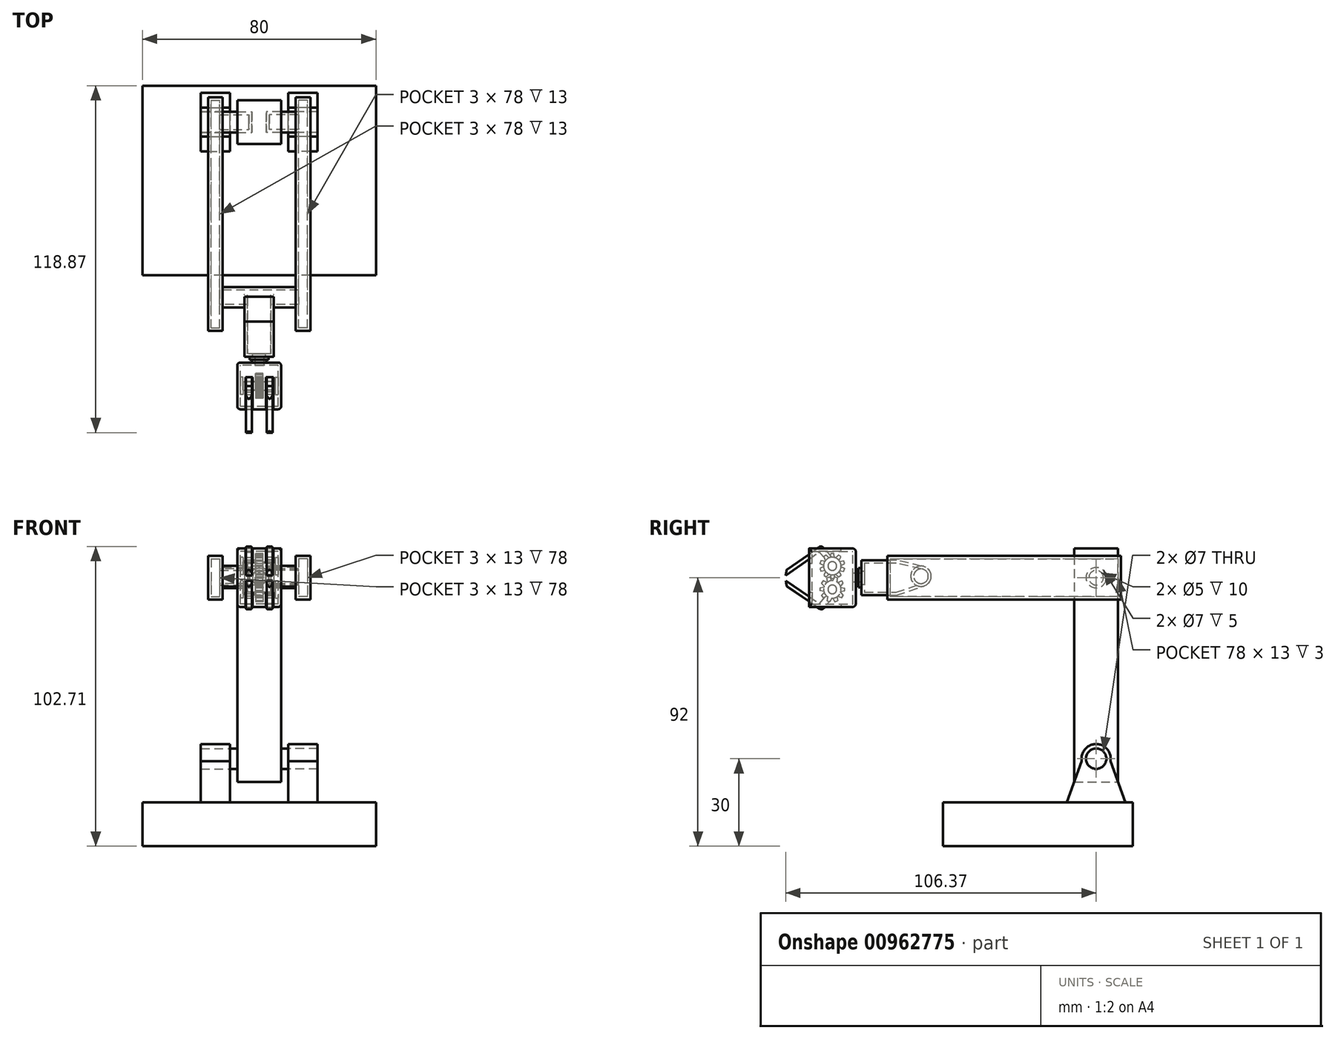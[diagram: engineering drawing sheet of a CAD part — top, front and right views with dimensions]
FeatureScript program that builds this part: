
annotation { "Feature Type Name" : "Feature", "Feature Type Description" : "" }
export const myFeature = defineFeature(function(context is Context, id is Id, definition is map)
    precondition{}
    {
        {
            var Q0;
            Q0=qCreatedBy(makeId("Top.planeOp"),FACE);
            var sketch = newSketch(context, id + "F0", { "sketchPlane" : qUnion([Q0])});
            skLineSegment(sketch, "E0.bottom", {"start": v(40, -32.5) * mm, "end": v(-40, -32.5) * mm});
            skLineSegment(sketch, "E0.top", {"start": v(40, 32.5) * mm, "end": v(-40, 32.5) * mm});
            skLineSegment(sketch, "E0.left", {"start": v(40, -32.5) * mm, "end": v(40, 32.5) * mm});
            skLineSegment(sketch, "E0.right", {"start": v(-40, -32.5) * mm, "end": v(-40, 32.5) * mm});
            skPoint(sketch, "E0.middle", {"position": v(0, 0) * mm});
            skSolve(sketch);
        }
        {
            var Q0;
            Q0=qSketchRegion(id+"F0",true);
            extrude(context, id + "F1", {"entities" : qUnion([Q0]), "depth" : 15 * mm, "offsetDistance" : 25 * mm});
        }
        {
            var Q0;
            Q0=qCreatedBy(makeId("Right.planeOp"),FACE);
            cPlane(context, id + "F2", {"entities" : qUnion([Q0]), "cplaneType" : CPlaneType.OFFSET, "offset" : 10 * mm, "width" : 150 * mm, "height" : 150 * mm});
        }
        {
            var Q0;
            Q0=qCreatedBy(id+"F2.planeOp",FACE);
            var sketch = newSketch(context, id + "F3", { "sketchPlane" : qUnion([Q0])});
            skCircle(sketch, "E1", {"center": v(20, 30) * mm, "radius": 5 * mm});
            skLineSegment(sketch, "E2", {"start": v(15.08, 29.11) * mm, "end": v(10, 15) * mm});
            skLineSegment(sketch, "E3", {"start": v(20, 30) * mm, "end": v(20, 15) * mm, "construction": true});
            skLineSegment(sketch, "E4.MirrorCS", {"start": v(24.92, 29.11) * mm, "end": v(30, 15) * mm});
            skLineSegment(sketch, "E5", {"start": v(10, 15) * mm, "end": v(30, 15) * mm});
            skCircle(sketch, "E6", {"center": v(20, 30) * mm, "radius": 3.5 * mm});
            skSolve(sketch);
        }
        {
            var Q0;
            Q0=qSketchRegion(id+"F3",true);
            extrude(context, id + "F4", {"entities" : qUnion([Q0]), "depth" : 10 * mm, "offsetDistance" : 25 * mm});
        }
        {
            var Q0;
            Q0=makeQuery(id+"F4.opExtrude","SWEPT_BODY",BODY,{"disambiguationData":[OSD([sQuery(id+"F3.wireOp",EDGE,"E1"),sQuery(id+"F3.wireOp",EDGE,"E2"),sQuery(id+"F3.wireOp",EDGE,"E4.MirrorCS"),sQuery(id+"F3.wireOp",EDGE,"E5"),sQuery(id+"F3.wireOp",EDGE,"E6")])]});
            var Q1;
            Q1=qCreatedBy(makeId("Right.planeOp"),FACE);
            mirror(context, id + "F5", {"operationType" : NewBodyOperationType.ADD, "entities" : qUnion([Q0]), "mirrorPlane" : qUnion([Q1])});
        }
        {
            var Q0;
            Q0=qCreatedBy(makeId("Right.planeOp"),FACE);
            var sketch = newSketch(context, id + "F6", { "sketchPlane" : qUnion([Q0])});
            skCircle(sketch, "E7.0", {"center": v(20, 30) * mm, "radius": 3.5 * mm});
            skSolve(sketch);
        }
        {
            var Q0;
            Q0=qSketchRegion(id+"F6",true);
            extrude(context, id + "F7", {"entities" : qUnion([Q0]), "endBound" : BoundingType.SYMMETRIC, "depth" : 40 * mm, "offsetDistance" : 25 * mm});
        }
        {
            var Q0;
            Q0=qCreatedBy(makeId("Right.planeOp"),FACE);
            var sketch = newSketch(context, id + "F8", { "sketchPlane" : qUnion([Q0])});
            skLineSegment(sketch, "E8", {"start": v(12.5, 22) * mm, "end": v(27.5, 22) * mm});
            skLineSegment(sketch, "E9", {"start": v(27.5, 22) * mm, "end": v(27.5, 102) * mm});
            skLineSegment(sketch, "E10", {"start": v(27.5, 102) * mm, "end": v(12.5, 102) * mm});
            skLineSegment(sketch, "E11", {"start": v(12.5, 102) * mm, "end": v(12.5, 22) * mm});
            skSolve(sketch);
        }
        {
            var Q0;
            Q0=qSketchRegion(id+"F8",true);
            extrude(context, id + "F9", {"entities" : qUnion([Q0]), "operationType" : NewBodyOperationType.ADD, "endBound" : BoundingType.SYMMETRIC, "depth" : 15 * mm, "offsetDistance" : 25 * mm});
        }
        {
            var Q0;
            Q0=makeQuery(id+"F9.opExtrude","CAP_FACE",FACE,{"disambiguationData":[OSD([sQuery(id+"F8.wireOp",EDGE,"E8"),sQuery(id+"F8.wireOp",EDGE,"E9"),sQuery(id+"F8.wireOp",EDGE,"E10"),sQuery(id+"F8.wireOp",EDGE,"E11")])],"isStart":false});
            var sketch = newSketch(context, id + "F10", { "sketchPlane" : qUnion([Q0])});
            skCircle(sketch, "E12", {"center": v(20, 92) * mm, "radius": 3.5 * mm});
            skSolve(sketch);
        }
        {
            var Q0;
            Q0=qSketchRegion(id+"F10",true);
            extrude(context, id + "F11", {"entities" : qUnion([Q0]), "operationType" : NewBodyOperationType.REMOVE, "oppositeDirection" : true, "depth" : 5 * mm, "offsetDistance" : 25 * mm});
        }
        {
            var Q0;
            Q0=makeQuery(id+"F9.opExtrude","CAP_FACE",FACE,{"disambiguationData":[OSD([sQuery(id+"F8.wireOp",EDGE,"E8"),sQuery(id+"F8.wireOp",EDGE,"E9"),sQuery(id+"F8.wireOp",EDGE,"E10"),sQuery(id+"F8.wireOp",EDGE,"E11")])],"isStart":true});
            var sketch = newSketch(context, id + "F12", { "sketchPlane" : qUnion([Q0])});
            skCircle(sketch, "E13.0", {"center": v(-20, 92) * mm, "radius": 3.5 * mm});
            skSolve(sketch);
        }
        {
            var Q0;
            Q0=qSketchRegion(id+"F12",true);
            extrude(context, id + "F13", {"entities" : qUnion([Q0]), "operationType" : NewBodyOperationType.REMOVE, "oppositeDirection" : true, "depth" : 5 * mm, "offsetDistance" : 25 * mm});
        }
        {
            var Q0;
            Q0=makeQuery(id+"F11.boolean.opBoolean","COPY",FACE,{"derivedFrom":makeQuery(id+"F11.opExtrude","CAP_FACE",FACE,{"disambiguationData":[OSD([sQuery(id+"F10.wireOp",EDGE,"E12")])],"isStart":false})});
            extrude(context, id + "F14", {"entities" : qUnion([Q0]), "depth" : 10 * mm, "offsetDistance" : 25 * mm});
        }
        {
            var Q0;
            Q0=makeQuery(id+"F14.opExtrude","CAP_FACE",FACE,{"disambiguationData":[OSD([sQuery(id+"F10.wireOp",EDGE,"E12")])],"isStart":false});
            var sketch = newSketch(context, id + "F15", { "sketchPlane" : qUnion([Q0])});
            skLineSegment(sketch, "E14", {"start": v(28.5, 99.5) * mm, "end": v(28.5, 84.5) * mm});
            skLineSegment(sketch, "E15", {"start": v(28.5, 84.5) * mm, "end": v(-51.5, 84.5) * mm});
            skLineSegment(sketch, "E16", {"start": v(-51.5, 84.5) * mm, "end": v(-51.5, 99.5) * mm});
            skLineSegment(sketch, "E17", {"start": v(-51.5, 99.5) * mm, "end": v(28.5, 99.5) * mm});
            skSolve(sketch);
        }
        {
            var Q0;
            Q0=qSketchRegion(id+"F15",true);
            extrude(context, id + "F16", {"entities" : qUnion([Q0]), "operationType" : NewBodyOperationType.ADD, "depth" : 5 * mm, "offsetDistance" : 25 * mm});
        }
        {
            var Q0;
            Q0=makeQuery(id+"F14.opExtrude","SWEPT_BODY",BODY,{"disambiguationData":[OSD([sQuery(id+"F10.wireOp",EDGE,"E12")])]});
            var Q1;
            Q1=qCreatedBy(makeId("Right.planeOp"),FACE);
            mirror(context, id + "F17", {"entities" : qUnion([Q0]), "mirrorPlane" : qUnion([Q1])});
        }
        {
            var Q0;
            Q0=qCreatedBy(makeId("Right.planeOp"),FACE);
            var sketch = newSketch(context, id + "F18", { "sketchPlane" : qUnion([Q0])});
            skCircle(sketch, "E18", {"center": v(-40, 92.5) * mm, "radius": 3.5 * mm});
            skLineSegment(sketch, "E19", {"start": v(-38.63, 95.72) * mm, "end": v(-48.37, 98) * mm});
            skLineSegment(sketch, "E20", {"start": v(-48.37, 98) * mm, "end": v(-60.37, 98) * mm});
            skLineSegment(sketch, "E21", {"start": v(-60.37, 98) * mm, "end": v(-60.37, 86) * mm});
            skLineSegment(sketch, "E22", {"start": v(-60.37, 86) * mm, "end": v(-48.37, 86) * mm});
            skLineSegment(sketch, "E23", {"start": v(-48.37, 86) * mm, "end": v(-38.89, 89.18) * mm});
            skSolve(sketch);
        }
        {
            var Q0;
            Q0=qSketchRegion(id+"F18",true);
            extrude(context, id + "F19", {"entities" : qUnion([Q0]), "endBound" : BoundingType.SYMMETRIC, "depth" : 10 * mm, "offsetDistance" : 25 * mm});
        }
        {
            var Q0;
            Q0=makeQuery(id+"F16.opExtrude","CAP_FACE",FACE,{"disambiguationData":[OSD([sQuery(id+"F15.wireOp",EDGE,"E14"),sQuery(id+"F15.wireOp",EDGE,"E15"),sQuery(id+"F15.wireOp",EDGE,"E16"),sQuery(id+"F15.wireOp",EDGE,"E17")])],"isStart":true});
            var sketch = newSketch(context, id + "F20", { "sketchPlane" : qUnion([Q0])});
            skCircle(sketch, "E24.0", {"center": v(40, 92.5) * mm, "radius": 3.5 * mm});
            skSolve(sketch);
        }
        {
            var Q0;
            Q0=qSketchRegion(id+"F20",true);
            extrude(context, id + "F21", {"entities" : qUnion([Q0]), "operationType" : NewBodyOperationType.REMOVE, "oppositeDirection" : true, "depth" : 3 * mm, "offsetDistance" : 25 * mm});
        }
        {
            var Q0;
            Q0=makeQuery(id+"F17.opPattern","COPY",FACE,{"derivedFrom":makeQuery(id+"F16.opExtrude","CAP_FACE",FACE,{"disambiguationData":[OSD([sQuery(id+"F15.wireOp",EDGE,"E14"),sQuery(id+"F15.wireOp",EDGE,"E15"),sQuery(id+"F15.wireOp",EDGE,"E16"),sQuery(id+"F15.wireOp",EDGE,"E17")])],"isStart":true}),"instanceName":"1"});
            var sketch = newSketch(context, id + "F22", { "sketchPlane" : qUnion([Q0])});
            skCircle(sketch, "E25.0", {"center": v(-40, 92.5) * mm, "radius": 3.5 * mm});
            skSolve(sketch);
        }
        {
            var Q0;
            Q0=qSketchRegion(id+"F22",true);
            extrude(context, id + "F23", {"entities" : qUnion([Q0]), "operationType" : NewBodyOperationType.REMOVE, "oppositeDirection" : true, "depth" : 3 * mm, "offsetDistance" : 25 * mm});
        }
        {
            var Q0;
            Q0=qCreatedBy(makeId("Right.planeOp"),FACE);
            var sketch = newSketch(context, id + "F24", { "sketchPlane" : qUnion([Q0])});
            skCircle(sketch, "E26.0", {"center": v(-40, 92.5) * mm, "radius": 3.5 * mm});
            skSolve(sketch);
        }
        {
            var Q0;
            Q0=qSketchRegion(id+"F24",true);
            extrude(context, id + "F25", {"entities" : qUnion([Q0]), "operationType" : NewBodyOperationType.ADD, "endBound" : BoundingType.SYMMETRIC, "depth" : 31 * mm, "offsetDistance" : 25 * mm});
        }
        {
            var Q0;
            Q0=makeQuery(id+"F19.opExtrude","SWEPT_FACE",FACE,{"disambiguationData":[OSD([sQuery(id+"F18.wireOp",EDGE,"E21")])]});
            var sketch = newSketch(context, id + "F26", { "sketchPlane" : qUnion([Q0])});
            skCircle(sketch, "E27", {"center": v(0, 92) * mm, "radius": 2.5 * mm});
            skPoint(sketch, "E27.centerSnap0", {"position": v(5, 92) * mm});
            skCircle(sketch, "E28", {"center": v(0, 92) * mm, "radius": 3.25 * mm});
            skSolve(sketch);
        }
        {
            var Q0;
            Q0=qSketchRegion(id+"F26",true);
            extrude(context, id + "F27", {"entities" : qUnion([Q0]), "operationType" : NewBodyOperationType.ADD, "depth" : 1 * mm, "offsetDistance" : 25 * mm});
        }
        {
            var Q0;
            Q0=makeQuery(id+"F27.boolean.opBoolean","SPLIT",FACE,{"disambiguationData":[TD([makeQuery(id+"F27.opExtrude","SWEPT_FACE",FACE,{"disambiguationData":[OSD([sQuery(id+"F26.wireOp",EDGE,"E27")])]})])],"derivedFrom":makeQuery(id+"F19.opExtrude","SWEPT_FACE",FACE,{"disambiguationData":[OSD([sQuery(id+"F18.wireOp",EDGE,"E21")])]})});
            extrude(context, id + "F28", {"entities" : qUnion([Q0]), "operationType" : NewBodyOperationType.REMOVE, "oppositeDirection" : true, "depth" : 5 * mm, "offsetDistance" : 25 * mm});
        }
        {
            var Q0;
            {var subQ0=sQuery(id+"F18.wireOp",EDGE,"E20");var subQ3=sQuery(id+"F18.wireOp",EDGE,"E21");Q0=makeQuery(id+"F27.boolean.opBoolean","SPLIT",FACE,{"disambiguationData":[TD([makeQuery(id+"F19.opExtrude","SWEPT_FACE",FACE,{"disambiguationData":[OSD([subQ0])]})])],"derivedFrom":makeQuery(id+"F19.opExtrude","SWEPT_FACE",FACE,{"disambiguationData":[OSD([subQ3])]})});}
            cPlane(context, id + "F29", {"entities" : qUnion([Q0]), "cplaneType" : CPlaneType.OFFSET, "offset" : 2 * mm, "width" : 150 * mm, "height" : 150 * mm});
        }
        {
            var Q0;
            Q0=qCreatedBy(id+"F29.planeOp",FACE);
            var sketch = newSketch(context, id + "F30", { "sketchPlane" : qUnion([Q0])});
            skLineSegment(sketch, "E29.bottom", {"start": v(7.5, 82) * mm, "end": v(-7.5, 82) * mm});
            skLineSegment(sketch, "E29.top", {"start": v(7.5, 102) * mm, "end": v(-7.5, 102) * mm});
            skLineSegment(sketch, "E29.left", {"start": v(7.5, 82) * mm, "end": v(7.5, 102) * mm});
            skLineSegment(sketch, "E29.right", {"start": v(-7.5, 82) * mm, "end": v(-7.5, 102) * mm});
            skPoint(sketch, "E29.middle", {"position": v(0, 92) * mm});
            skSolve(sketch);
        }
        {
            var Q0;
            Q0=qSketchRegion(id+"F30",true);
            extrude(context, id + "F31", {"entities" : qUnion([Q0]), "depth" : 15 * mm, "offsetDistance" : 25 * mm});
        }
        {
            var Q0;
            Q0=makeQuery(id+"F31.opExtrude","CAP_FACE",FACE,{"disambiguationData":[OSD([sQuery(id+"F30.wireOp",EDGE,"E29.bottom"),sQuery(id+"F30.wireOp",EDGE,"E29.top"),sQuery(id+"F30.wireOp",EDGE,"E29.left"),sQuery(id+"F30.wireOp",EDGE,"E29.right")])],"isStart":true});
            var sketch = newSketch(context, id + "F32", { "sketchPlane" : qUnion([Q0])});
            skCircle(sketch, "E30.0", {"center": v(0, 92) * mm, "radius": 2.5 * mm});
            skSolve(sketch);
        }
        {
            var Q0;
            Q0=qSketchRegion(id+"F32",true);
            extrude(context, id + "F33", {"entities" : qUnion([Q0]), "operationType" : NewBodyOperationType.ADD, "endBound" : BoundingType.UP_TO_NEXT, "depth" : 25 * mm, "offsetDistance" : 25 * mm});
        }
        {
            var Q0;
            Q0=makeQuery(id+"F31.opExtrude","CAP_FACE",FACE,{"disambiguationData":[OSD([sQuery(id+"F30.wireOp",EDGE,"E29.bottom"),sQuery(id+"F30.wireOp",EDGE,"E29.top"),sQuery(id+"F30.wireOp",EDGE,"E29.left"),sQuery(id+"F30.wireOp",EDGE,"E29.right")])],"isStart":false});
            shell(context, id + "F34", {"entities" : qUnion([Q0]), "thickness" : 1 * mm});
        }
        {
            var Q0;
            Q0=makeQuery(id+"F34.opShell","OFFSET_FACE",FACE,{"disambiguationData":[OSD([sQuery(id+"F30.wireOp",EDGE,"E29.right")])]});
            var sketch = newSketch(context, id + "F35", { "sketchPlane" : qUnion([Q0])});
            skCircle(sketch, "E31", {"center": v(-70.37, 96) * mm, "radius": 3 * mm});
            skCircle(sketch, "E32", {"center": v(-70.37, 96) * mm, "radius": 1.5 * mm});
            skSolve(sketch);
        }
        {
            var Q0;
            Q0=qSketchRegion(id+"F35",true);
            extrude(context, id + "F36", {"entities" : qUnion([Q0]), "operationType" : NewBodyOperationType.ADD, "depth" : 1 * mm, "offsetDistance" : 25 * mm});
        }
        {
            var Q0;
            Q0=makeQuery(id+"F34.opShell","OFFSET_FACE",FACE,{"disambiguationData":[OSD([sQuery(id+"F30.wireOp",EDGE,"E29.left")])]});
            var sketch = newSketch(context, id + "F37", { "sketchPlane" : qUnion([Q0])});
            skCircle(sketch, "E33.0", {"center": v(70.37, 96) * mm, "radius": 3 * mm});
            skCircle(sketch, "E34.0", {"center": v(70.37, 96) * mm, "radius": 1.5 * mm});
            skSolve(sketch);
        }
        {
            var Q0;
            Q0=qSketchRegion(id+"F37",true);
            extrude(context, id + "F38", {"entities" : qUnion([Q0]), "operationType" : NewBodyOperationType.ADD, "depth" : 1 * mm, "offsetDistance" : 25 * mm});
        }
        {
            var Q0;
            Q0=makeQuery(id+"F35.imprint","IMPRINT",FACE,{"disambiguationData":[TD([[makeQuery(id+"F35.imprint","IMPRINT",EDGE,{"derivedFrom":sQuery(id+"F35.wireOp",EDGE,"E31")}),-1.0]])]});
            var sketch = newSketch(context, id + "F39", { "sketchPlane" : qUnion([Q0])});
            skCircle(sketch, "E35", {"center": v(-70.37, 88) * mm, "radius": 1.5 * mm});
            skCircle(sketch, "E36", {"center": v(-70.37, 88) * mm, "radius": 3 * mm});
            skSolve(sketch);
        }
        {
            var Q0;
            Q0=qSketchRegion(id+"F39",true);
            extrude(context, id + "F40", {"entities" : qUnion([Q0]), "operationType" : NewBodyOperationType.ADD, "depth" : 1 * mm, "offsetDistance" : 25 * mm});
        }
        {
            var Q0;
            {var subQ1=sQuery(id+"F30.wireOp",EDGE,"E29.left");var subQ3=sQuery(id+"F30.wireOp",EDGE,"E29.bottom");Q0=makeQuery(id+"F38.boolean.opBoolean","SPLIT",FACE,{"disambiguationData":[TD([makeQuery(id+"F34.opShell","OFFSET_FACE",FACE,{"disambiguationData":[OSD([subQ3])]})])],"derivedFrom":makeQuery(id+"F34.opShell","OFFSET_FACE",FACE,{"disambiguationData":[OSD([subQ1])]})});}
            var sketch = newSketch(context, id + "F41", { "sketchPlane" : qUnion([Q0])});
            skCircle(sketch, "E37.0", {"center": v(70.37, 88) * mm, "radius": 3 * mm});
            skCircle(sketch, "E38.0", {"center": v(70.37, 88) * mm, "radius": 1.5 * mm});
            skSolve(sketch);
        }
        {
            var Q0;
            Q0=qSketchRegion(id+"F41",true);
            extrude(context, id + "F42", {"entities" : qUnion([Q0]), "operationType" : NewBodyOperationType.ADD, "depth" : 1 * mm, "offsetDistance" : 25 * mm});
        }
        {
            var Q0;
            Q0=qCreatedBy(makeId("Right.planeOp"),FACE);
            var sketch = newSketch(context, id + "F43", { "sketchPlane" : qUnion([Q0])});
            skCircle(sketch, "E39.0", {"center": v(-70.37, 96) * mm, "radius": 3 * mm});
            skLineSegment(sketch, "E40", {"start": v(-70.37, 96) * mm, "end": v(-70.37, 99) * mm, "construction": true});
            skLineSegment(sketch, "E41", {"start": v(-69.62, 98.9) * mm, "end": v(-69.87, 100.29) * mm});
            skLineSegment(sketch, "E42", {"start": v(-69.87, 100.29) * mm, "end": v(-70.37, 100.29) * mm});
            skLineSegment(sketch, "E43.MirrorCS", {"start": v(-70.87, 100.29) * mm, "end": v(-70.37, 100.29) * mm});
            skLineSegment(sketch, "E44.MirrorCS", {"start": v(-71.1, 98.9) * mm, "end": v(-70.87, 100.29) * mm});
            skLineSegment(sketch, "E45.1.0", {"start": v(-72.68, 97.91) * mm, "end": v(-73.29, 99.17) * mm});
            skLineSegment(sketch, "E45.1.1", {"start": v(-73.29, 99.17) * mm, "end": v(-72.89, 99.47) * mm});
            skLineSegment(sketch, "E45.1.2", {"start": v(-72.48, 99.76) * mm, "end": v(-72.89, 99.47) * mm});
            skLineSegment(sketch, "E45.1.3", {"start": v(-71.47, 98.79) * mm, "end": v(-72.48, 99.76) * mm});
            skLineSegment(sketch, "E45.2.0", {"start": v(-73.36, 96.2) * mm, "end": v(-74.6, 96.85) * mm});
            skLineSegment(sketch, "E45.2.1", {"start": v(-74.6, 96.85) * mm, "end": v(-74.44, 97.32) * mm});
            skLineSegment(sketch, "E45.2.2", {"start": v(-74.29, 97.8) * mm, "end": v(-74.44, 97.32) * mm});
            skLineSegment(sketch, "E45.2.3", {"start": v(-72.9, 97.6) * mm, "end": v(-74.29, 97.8) * mm});
            skLineSegment(sketch, "E46.1.3.0", {"start": v(-72.9, 94.4) * mm, "end": v(-74.29, 94.2) * mm});
            skLineSegment(sketch, "E46.3.3.0", {"start": v(-74.29, 94.2) * mm, "end": v(-74.44, 94.68) * mm});
            skLineSegment(sketch, "E46.6.3.0", {"start": v(-74.6, 95.15) * mm, "end": v(-74.44, 94.68) * mm});
            skLineSegment(sketch, "E46.9.3.0", {"start": v(-73.36, 95.8) * mm, "end": v(-74.6, 95.15) * mm});
            skLineSegment(sketch, "E46.1.4.0", {"start": v(-71.47, 93.21) * mm, "end": v(-72.48, 92.24) * mm});
            skLineSegment(sketch, "E46.3.4.0", {"start": v(-72.48, 92.24) * mm, "end": v(-72.89, 92.53) * mm});
            skLineSegment(sketch, "E46.6.4.0", {"start": v(-73.29, 92.83) * mm, "end": v(-72.89, 92.53) * mm});
            skLineSegment(sketch, "E46.9.4.0", {"start": v(-72.68, 94.09) * mm, "end": v(-73.29, 92.83) * mm});
            skLineSegment(sketch, "E46.1.5.0", {"start": v(-69.62, 93.1) * mm, "end": v(-69.87, 91.71) * mm});
            skLineSegment(sketch, "E46.3.5.0", {"start": v(-69.87, 91.71) * mm, "end": v(-70.37, 91.71) * mm});
            skLineSegment(sketch, "E46.6.5.0", {"start": v(-70.87, 91.71) * mm, "end": v(-70.37, 91.71) * mm});
            skLineSegment(sketch, "E46.9.5.0", {"start": v(-71.1, 93.1) * mm, "end": v(-70.87, 91.71) * mm});
            skLineSegment(sketch, "E46.1.6.0", {"start": v(-68.06, 94.09) * mm, "end": v(-67.44, 92.83) * mm});
            skLineSegment(sketch, "E46.3.6.0", {"start": v(-67.44, 92.83) * mm, "end": v(-67.85, 92.53) * mm});
            skLineSegment(sketch, "E46.6.6.0", {"start": v(-68.25, 92.24) * mm, "end": v(-67.85, 92.53) * mm});
            skLineSegment(sketch, "E46.9.6.0", {"start": v(-69.26, 93.21) * mm, "end": v(-68.25, 92.24) * mm});
            skLineSegment(sketch, "E46.1.7.0", {"start": v(-67.37, 95.8) * mm, "end": v(-66.14, 95.15) * mm});
            skLineSegment(sketch, "E46.3.7.0", {"start": v(-66.14, 95.15) * mm, "end": v(-66.3, 94.68) * mm});
            skLineSegment(sketch, "E46.6.7.0", {"start": v(-66.45, 94.2) * mm, "end": v(-66.3, 94.68) * mm});
            skLineSegment(sketch, "E46.9.7.0", {"start": v(-67.83, 94.4) * mm, "end": v(-66.45, 94.2) * mm});
            skLineSegment(sketch, "E46.1.8.0", {"start": v(-67.83, 97.6) * mm, "end": v(-66.45, 97.8) * mm});
            skLineSegment(sketch, "E46.3.8.0", {"start": v(-66.45, 97.8) * mm, "end": v(-66.3, 97.32) * mm});
            skLineSegment(sketch, "E46.6.8.0", {"start": v(-66.14, 96.85) * mm, "end": v(-66.3, 97.32) * mm});
            skLineSegment(sketch, "E46.9.8.0", {"start": v(-67.37, 96.2) * mm, "end": v(-66.14, 96.85) * mm});
            skLineSegment(sketch, "E46.1.9.0", {"start": v(-69.26, 98.79) * mm, "end": v(-68.25, 99.76) * mm});
            skLineSegment(sketch, "E46.3.9.0", {"start": v(-68.25, 99.76) * mm, "end": v(-67.85, 99.47) * mm});
            skLineSegment(sketch, "E46.6.9.0", {"start": v(-67.44, 99.17) * mm, "end": v(-67.85, 99.47) * mm});
            skLineSegment(sketch, "E46.9.9.0", {"start": v(-68.06, 97.91) * mm, "end": v(-67.44, 99.17) * mm});
            skSolve(sketch);
        }
        {
            var Q0;
            Q0=qSketchRegion(id+"F43",true);
            extrude(context, id + "F44", {"entities" : qUnion([Q0]), "endBound" : BoundingType.SYMMETRIC, "depth" : 2.5 * mm, "offsetDistance" : 25 * mm});
        }
        {
            var Q0;
            Q0=makeQuery(id+"F38.boolean.opBoolean","SPLIT",FACE,{"disambiguationData":[TD([makeQuery(id+"F38.opExtrude","SWEPT_FACE",FACE,{"disambiguationData":[OSD([sQuery(id+"F37.wireOp",EDGE,"E34.0")])]})])],"derivedFrom":makeQuery(id+"F34.opShell","OFFSET_FACE",FACE,{"disambiguationData":[OSD([sQuery(id+"F30.wireOp",EDGE,"E29.left")])]})});
            extrude(context, id + "F45", {"entities" : qUnion([Q0]), "operationType" : NewBodyOperationType.ADD, "depth" : 13 * mm, "offsetDistance" : 25 * mm});
        }
        {
            var Q0;
            Q0=qCreatedBy(makeId("Right.planeOp"),FACE);
            var sketch = newSketch(context, id + "F46", { "sketchPlane" : qUnion([Q0])});
            skCircle(sketch, "E47.0", {"center": v(-70.37, 88) * mm, "radius": 3 * mm});
            skLineSegment(sketch, "E48", {"start": v(-70.37, 88) * mm, "end": v(-67.37, 88) * mm, "construction": true});
            skLineSegment(sketch, "E49", {"start": v(-67.46, 87.26) * mm, "end": v(-66.08, 87.5) * mm});
            skLineSegment(sketch, "E50", {"start": v(-66.08, 87.5) * mm, "end": v(-66.08, 88) * mm});
            skLineSegment(sketch, "E51.MirrorCS", {"start": v(-67.46, 88.74) * mm, "end": v(-66.08, 88.5) * mm});
            skLineSegment(sketch, "E52.MirrorCS", {"start": v(-66.08, 88.5) * mm, "end": v(-66.08, 88) * mm});
            skLineSegment(sketch, "E53.1.0", {"start": v(-68.45, 90.3) * mm, "end": v(-67.2, 90.92) * mm});
            skLineSegment(sketch, "E53.1.1", {"start": v(-67.2, 90.92) * mm, "end": v(-66.9, 90.52) * mm});
            skLineSegment(sketch, "E53.1.2", {"start": v(-66.6, 90.11) * mm, "end": v(-66.9, 90.52) * mm});
            skLineSegment(sketch, "E53.1.3", {"start": v(-67.58, 89.1) * mm, "end": v(-66.6, 90.11) * mm});
            skLineSegment(sketch, "E53.2.0", {"start": v(-70.18, 91) * mm, "end": v(-69.52, 92.23) * mm});
            skLineSegment(sketch, "E53.2.1", {"start": v(-69.52, 92.23) * mm, "end": v(-69.04, 92.08) * mm});
            skLineSegment(sketch, "E53.2.2", {"start": v(-68.57, 91.92) * mm, "end": v(-69.04, 92.08) * mm});
            skLineSegment(sketch, "E53.2.3", {"start": v(-68.76, 90.53) * mm, "end": v(-68.57, 91.92) * mm});
            skLineSegment(sketch, "E54.1.3.0", {"start": v(-71.97, 90.53) * mm, "end": v(-72.17, 91.92) * mm});
            skLineSegment(sketch, "E54.3.3.0", {"start": v(-72.17, 91.92) * mm, "end": v(-71.7, 92.08) * mm});
            skLineSegment(sketch, "E54.6.3.0", {"start": v(-71.22, 92.23) * mm, "end": v(-71.7, 92.08) * mm});
            skLineSegment(sketch, "E54.9.3.0", {"start": v(-70.56, 91) * mm, "end": v(-71.22, 92.23) * mm});
            skLineSegment(sketch, "E54.1.4.0", {"start": v(-73.15, 89.1) * mm, "end": v(-74.13, 90.11) * mm});
            skLineSegment(sketch, "E54.3.4.0", {"start": v(-74.13, 90.11) * mm, "end": v(-73.83, 90.52) * mm});
            skLineSegment(sketch, "E54.6.4.0", {"start": v(-73.54, 90.92) * mm, "end": v(-73.83, 90.52) * mm});
            skLineSegment(sketch, "E54.9.4.0", {"start": v(-72.28, 90.3) * mm, "end": v(-73.54, 90.92) * mm});
            skLineSegment(sketch, "E54.1.5.0", {"start": v(-73.27, 87.26) * mm, "end": v(-74.65, 87.5) * mm});
            skLineSegment(sketch, "E54.3.5.0", {"start": v(-74.65, 87.5) * mm, "end": v(-74.65, 88) * mm});
            skLineSegment(sketch, "E54.6.5.0", {"start": v(-74.65, 88.5) * mm, "end": v(-74.65, 88) * mm});
            skLineSegment(sketch, "E54.9.5.0", {"start": v(-73.27, 88.74) * mm, "end": v(-74.65, 88.5) * mm});
            skLineSegment(sketch, "E54.1.6.0", {"start": v(-72.28, 85.7) * mm, "end": v(-73.54, 85.08) * mm});
            skLineSegment(sketch, "E54.3.6.0", {"start": v(-73.54, 85.08) * mm, "end": v(-73.83, 85.48) * mm});
            skLineSegment(sketch, "E54.6.6.0", {"start": v(-74.13, 85.89) * mm, "end": v(-73.83, 85.48) * mm});
            skLineSegment(sketch, "E54.9.6.0", {"start": v(-73.15, 86.9) * mm, "end": v(-74.13, 85.89) * mm});
            skLineSegment(sketch, "E54.1.7.0", {"start": v(-70.56, 85) * mm, "end": v(-71.22, 83.77) * mm});
            skLineSegment(sketch, "E54.3.7.0", {"start": v(-71.22, 83.77) * mm, "end": v(-71.7, 83.92) * mm});
            skLineSegment(sketch, "E54.6.7.0", {"start": v(-72.17, 84.08) * mm, "end": v(-71.7, 83.92) * mm});
            skLineSegment(sketch, "E54.9.7.0", {"start": v(-71.97, 85.47) * mm, "end": v(-72.17, 84.08) * mm});
            skLineSegment(sketch, "E54.1.8.0", {"start": v(-68.76, 85.47) * mm, "end": v(-68.57, 84.08) * mm});
            skLineSegment(sketch, "E54.3.8.0", {"start": v(-68.57, 84.08) * mm, "end": v(-69.04, 83.92) * mm});
            skLineSegment(sketch, "E54.6.8.0", {"start": v(-69.52, 83.77) * mm, "end": v(-69.04, 83.92) * mm});
            skLineSegment(sketch, "E54.9.8.0", {"start": v(-70.18, 85) * mm, "end": v(-69.52, 83.77) * mm});
            skLineSegment(sketch, "E54.1.9.0", {"start": v(-67.58, 86.9) * mm, "end": v(-66.6, 85.89) * mm});
            skLineSegment(sketch, "E54.3.9.0", {"start": v(-66.6, 85.89) * mm, "end": v(-66.9, 85.48) * mm});
            skLineSegment(sketch, "E54.6.9.0", {"start": v(-67.2, 85.08) * mm, "end": v(-66.9, 85.48) * mm});
            skLineSegment(sketch, "E54.9.9.0", {"start": v(-68.45, 85.7) * mm, "end": v(-67.2, 85.08) * mm});
            skSolve(sketch);
        }
        {
            var Q0;
            Q0=qSketchRegion(id+"F46",true);
            extrude(context, id + "F47", {"entities" : qUnion([Q0]), "endBound" : BoundingType.SYMMETRIC, "depth" : 2.5 * mm, "offsetDistance" : 25 * mm});
        }
        {
            var Q0;
            Q0=makeQuery(id+"F39.imprint","IMPRINT",FACE,{"disambiguationData":[TD([[makeQuery(id+"F39.imprint","IMPRINT",EDGE,{"derivedFrom":sQuery(id+"F39.wireOp",EDGE,"E35")}),1.0]])]});
            extrude(context, id + "F48", {"entities" : qUnion([Q0]), "operationType" : NewBodyOperationType.ADD, "depth" : 13 * mm, "offsetDistance" : 25 * mm});
        }
        {
            var Q0;
            Q0=makeQuery(id+"F31.opExtrude","SWEPT_FACE",FACE,{"disambiguationData":[OSD([sQuery(id+"F30.wireOp",EDGE,"E29.top")])]});
            var sketch = newSketch(context, id + "F49", { "sketchPlane" : qUnion([Q0])});
            skLineSegment(sketch, "E55", {"start": v(2.3, -77.37) * mm, "end": v(2.3, -67.37) * mm});
            skLineSegment(sketch, "E56", {"start": v(2.3, -67.37) * mm, "end": v(4.8, -67.37) * mm});
            skLineSegment(sketch, "E57", {"start": v(4.8, -67.37) * mm, "end": v(4.8, -77.37) * mm});
            skLineSegment(sketch, "E58.1.0.0", {"start": v(-4.7, -77.37) * mm, "end": v(-4.7, -67.37) * mm});
            skLineSegment(sketch, "E58.1.0.1", {"start": v(-4.7, -67.37) * mm, "end": v(-2.2, -67.37) * mm});
            skLineSegment(sketch, "E58.1.0.2", {"start": v(-2.2, -67.37) * mm, "end": v(-2.2, -77.37) * mm});
            skLineSegment(sketch, "E58.direction1", {"start": v(2.3, -77.37) * mm, "end": v(-4.7, -77.37) * mm, "construction": true});
            skSolve(sketch);
        }
        {
            var Q0;
            {var subQ0=sQuery(id+"F49.wireOp",EDGE,"E58.1.0.0");Q0=makeQuery(id+"F49.imprint","IMPRINT",FACE,{"disambiguationData":[TD([[makeQuery(id+"F49.imprint","IMPRINT",EDGE,{"derivedFrom":subQ0}),-1.0]])]});}
            extrude(context, id + "F50", {"entities" : qUnion([Q0]), "operationType" : NewBodyOperationType.REMOVE, "oppositeDirection" : true, "depth" : 2 * mm, "offsetDistance" : 25 * mm});
        }
        {
            var Q0;
            {var subQ0=sQuery(id+"F49.wireOp",EDGE,"E55");Q0=makeQuery(id+"F49.imprint","IMPRINT",FACE,{"disambiguationData":[TD([[makeQuery(id+"F49.imprint","IMPRINT",EDGE,{"derivedFrom":subQ0}),-1.0]])]});}
            extrude(context, id + "F51", {"entities" : qUnion([Q0]), "operationType" : NewBodyOperationType.REMOVE, "oppositeDirection" : true, "depth" : 2 * mm, "offsetDistance" : 25 * mm});
        }
        {
            var Q0;
            Q0=makeQuery(id+"F44.opExtrude","CAP_FACE",FACE,{"disambiguationData":[OSD([sQuery(id+"F43.wireOp",EDGE,"E39.0"),sQuery(id+"F43.wireOp",EDGE,"E41"),sQuery(id+"F43.wireOp",EDGE,"E42"),sQuery(id+"F43.wireOp",EDGE,"E43.MirrorCS"),sQuery(id+"F43.wireOp",EDGE,"E44.MirrorCS"),sQuery(id+"F43.wireOp",EDGE,"E45.1.0"),sQuery(id+"F43.wireOp",EDGE,"E45.1.1"),sQuery(id+"F43.wireOp",EDGE,"E45.1.2"),sQuery(id+"F43.wireOp",EDGE,"E45.1.3"),sQuery(id+"F43.wireOp",EDGE,"E45.2.0"),sQuery(id+"F43.wireOp",EDGE,"E45.2.1"),sQuery(id+"F43.wireOp",EDGE,"E45.2.2"),sQuery(id+"F43.wireOp",EDGE,"E45.2.3"),sQuery(id+"F43.wireOp",EDGE,"E46.1.3.0"),sQuery(id+"F43.wireOp",EDGE,"E46.3.3.0"),sQuery(id+"F43.wireOp",EDGE,"E46.6.3.0"),sQuery(id+"F43.wireOp",EDGE,"E46.9.3.0"),sQuery(id+"F43.wireOp",EDGE,"E46.1.4.0"),sQuery(id+"F43.wireOp",EDGE,"E46.3.4.0"),sQuery(id+"F43.wireOp",EDGE,"E46.6.4.0"),sQuery(id+"F43.wireOp",EDGE,"E46.9.4.0"),sQuery(id+"F43.wireOp",EDGE,"E46.1.5.0"),sQuery(id+"F43.wireOp",EDGE,"E46.3.5.0"),sQuery(id+"F43.wireOp",EDGE,"E46.6.5.0"),sQuery(id+"F43.wireOp",EDGE,"E46.9.5.0"),sQuery(id+"F43.wireOp",EDGE,"E46.1.6.0"),sQuery(id+"F43.wireOp",EDGE,"E46.3.6.0"),sQuery(id+"F43.wireOp",EDGE,"E46.6.6.0"),sQuery(id+"F43.wireOp",EDGE,"E46.9.6.0"),sQuery(id+"F43.wireOp",EDGE,"E46.1.7.0"),sQuery(id+"F43.wireOp",EDGE,"E46.3.7.0"),sQuery(id+"F43.wireOp",EDGE,"E46.6.7.0"),sQuery(id+"F43.wireOp",EDGE,"E46.9.7.0"),sQuery(id+"F43.wireOp",EDGE,"E46.1.8.0"),sQuery(id+"F43.wireOp",EDGE,"E46.3.8.0"),sQuery(id+"F43.wireOp",EDGE,"E46.6.8.0"),sQuery(id+"F43.wireOp",EDGE,"E46.9.8.0"),sQuery(id+"F43.wireOp",EDGE,"E46.1.9.0"),sQuery(id+"F43.wireOp",EDGE,"E46.3.9.0"),sQuery(id+"F43.wireOp",EDGE,"E46.6.9.0"),sQuery(id+"F43.wireOp",EDGE,"E46.9.9.0")])],"isStart":false});
            cPlane(context, id + "F52", {"entities" : qUnion([Q0]), "cplaneType" : CPlaneType.OFFSET, "offset" : 2.3 * mm, "width" : 150 * mm, "height" : 150 * mm});
        }
        {
            var Q0;
            Q0=qCreatedBy(id+"F52.planeOp",FACE);
            var sketch = newSketch(context, id + "F53", { "sketchPlane" : qUnion([Q0])});
            skCircle(sketch, "E59.0", {"center": v(-70.37, 96) * mm, "radius": 3 * mm});
            skCircle(sketch, "E60.0", {"center": v(-70.37, 96) * mm, "radius": 1.5 * mm});
            skLineSegment(sketch, "E61", {"start": v(-70.41, 99) * mm, "end": v(-74.16, 103.03) * mm});
            skLineSegment(sketch, "E62", {"start": v(-74.16, 103.03) * mm, "end": v(-86, 94.67) * mm});
            skLineSegment(sketch, "E63", {"start": v(-86.37, 92.7) * mm, "end": v(-74.92, 100.77) * mm});
            skLineSegment(sketch, "E64", {"start": v(-74.92, 100.77) * mm, "end": v(-72.47, 98.14) * mm});
            skLineSegment(sketch, "E65", {"start": v(-86, 94.67) * mm, "end": v(-86.37, 92.7) * mm});
            skSolve(sketch);
        }
        {
            var Q0;
            Q0=qSketchRegion(id+"F53",true);
            extrude(context, id + "F54", {"entities" : qUnion([Q0]), "endBound" : BoundingType.SYMMETRIC, "depth" : 2 * mm, "offsetDistance" : 25 * mm});
        }
        {
            var Q0;
            Q0=makeQuery(id+"F54.opExtrude","SWEPT_BODY",BODY,{"disambiguationData":[OSD([sQuery(id+"F53.wireOp",EDGE,"E59.0"),sQuery(id+"F53.wireOp",EDGE,"E60.0"),sQuery(id+"F53.wireOp",EDGE,"E61"),sQuery(id+"F53.wireOp",EDGE,"E62"),sQuery(id+"F53.wireOp",EDGE,"E63"),sQuery(id+"F53.wireOp",EDGE,"E64"),sQuery(id+"F53.wireOp",EDGE,"E65")])]});
            var Q1;
            Q1=qCreatedBy(makeId("Right.planeOp"),FACE);
            mirror(context, id + "F55", {"entities" : qUnion([Q0]), "mirrorPlane" : qUnion([Q1])});
        }
        {
            var Q0;
            Q0=makeQuery(id+"F31.opExtrude","SWEPT_FACE",FACE,{"disambiguationData":[OSD([sQuery(id+"F30.wireOp",EDGE,"E29.bottom")])]});
            var sketch = newSketch(context, id + "F56", { "sketchPlane" : qUnion([Q0])});
            skLineSegment(sketch, "E66.0", {"start": v(-4.7, 77.37) * mm, "end": v(-4.7, 67.37) * mm});
            skLineSegment(sketch, "E67.0", {"start": v(-2.2, 67.37) * mm, "end": v(-2.2, 77.37) * mm});
            skLineSegment(sketch, "E68.0", {"start": v(-4.7, 67.37) * mm, "end": v(-2.2, 67.37) * mm});
            skLineSegment(sketch, "E69.0", {"start": v(2.3, 77.37) * mm, "end": v(2.3, 67.37) * mm});
            skLineSegment(sketch, "E70.0", {"start": v(2.3, 67.37) * mm, "end": v(4.8, 67.37) * mm});
            skLineSegment(sketch, "E71.0", {"start": v(4.8, 67.37) * mm, "end": v(4.8, 77.37) * mm});
            skSolve(sketch);
        }
        {
            var Q0;
            {var subQ0=sQuery(id+"F56.wireOp",EDGE,"E66.0");Q0=makeQuery(id+"F56.imprint","IMPRINT",FACE,{"disambiguationData":[TD([[makeQuery(id+"F56.imprint","IMPRINT",EDGE,{"derivedFrom":subQ0}),1.0]])]});}
            extrude(context, id + "F57", {"entities" : qUnion([Q0]), "operationType" : NewBodyOperationType.REMOVE, "oppositeDirection" : true, "depth" : 2 * mm, "offsetDistance" : 25 * mm});
        }
        {
            var Q0;
            {var subQ0=sQuery(id+"F56.wireOp",EDGE,"E69.0");Q0=makeQuery(id+"F56.imprint","IMPRINT",FACE,{"disambiguationData":[TD([[makeQuery(id+"F56.imprint","IMPRINT",EDGE,{"derivedFrom":subQ0}),1.0]])]});}
            extrude(context, id + "F58", {"entities" : qUnion([Q0]), "operationType" : NewBodyOperationType.REMOVE, "oppositeDirection" : true, "depth" : 2 * mm, "offsetDistance" : 25 * mm});
        }
        {
            var Q0;
            Q0=makeQuery(id+"F47.opExtrude","CAP_FACE",FACE,{"disambiguationData":[OSD([sQuery(id+"F46.wireOp",EDGE,"E47.0"),sQuery(id+"F46.wireOp",EDGE,"E49"),sQuery(id+"F46.wireOp",EDGE,"E50"),sQuery(id+"F46.wireOp",EDGE,"E51.MirrorCS"),sQuery(id+"F46.wireOp",EDGE,"E52.MirrorCS"),sQuery(id+"F46.wireOp",EDGE,"E53.1.0"),sQuery(id+"F46.wireOp",EDGE,"E53.1.1"),sQuery(id+"F46.wireOp",EDGE,"E53.1.2"),sQuery(id+"F46.wireOp",EDGE,"E53.1.3"),sQuery(id+"F46.wireOp",EDGE,"E53.2.0"),sQuery(id+"F46.wireOp",EDGE,"E53.2.1"),sQuery(id+"F46.wireOp",EDGE,"E53.2.2"),sQuery(id+"F46.wireOp",EDGE,"E53.2.3"),sQuery(id+"F46.wireOp",EDGE,"E54.1.3.0"),sQuery(id+"F46.wireOp",EDGE,"E54.3.3.0"),sQuery(id+"F46.wireOp",EDGE,"E54.6.3.0"),sQuery(id+"F46.wireOp",EDGE,"E54.9.3.0"),sQuery(id+"F46.wireOp",EDGE,"E54.1.4.0"),sQuery(id+"F46.wireOp",EDGE,"E54.3.4.0"),sQuery(id+"F46.wireOp",EDGE,"E54.6.4.0"),sQuery(id+"F46.wireOp",EDGE,"E54.9.4.0"),sQuery(id+"F46.wireOp",EDGE,"E54.1.5.0"),sQuery(id+"F46.wireOp",EDGE,"E54.3.5.0"),sQuery(id+"F46.wireOp",EDGE,"E54.6.5.0"),sQuery(id+"F46.wireOp",EDGE,"E54.9.5.0"),sQuery(id+"F46.wireOp",EDGE,"E54.1.6.0"),sQuery(id+"F46.wireOp",EDGE,"E54.3.6.0"),sQuery(id+"F46.wireOp",EDGE,"E54.6.6.0"),sQuery(id+"F46.wireOp",EDGE,"E54.9.6.0"),sQuery(id+"F46.wireOp",EDGE,"E54.1.7.0"),sQuery(id+"F46.wireOp",EDGE,"E54.3.7.0"),sQuery(id+"F46.wireOp",EDGE,"E54.6.7.0"),sQuery(id+"F46.wireOp",EDGE,"E54.9.7.0"),sQuery(id+"F46.wireOp",EDGE,"E54.1.8.0"),sQuery(id+"F46.wireOp",EDGE,"E54.3.8.0"),sQuery(id+"F46.wireOp",EDGE,"E54.6.8.0"),sQuery(id+"F46.wireOp",EDGE,"E54.9.8.0"),sQuery(id+"F46.wireOp",EDGE,"E54.1.9.0"),sQuery(id+"F46.wireOp",EDGE,"E54.3.9.0"),sQuery(id+"F46.wireOp",EDGE,"E54.6.9.0"),sQuery(id+"F46.wireOp",EDGE,"E54.9.9.0")])],"isStart":false});
            cPlane(context, id + "F59", {"entities" : qUnion([Q0]), "cplaneType" : CPlaneType.OFFSET, "offset" : 2.3 * mm, "width" : 150 * mm, "height" : 150 * mm});
        }
        {
            var Q0;
            Q0=qCreatedBy(id+"F59.planeOp",FACE);
            var sketch = newSketch(context, id + "F60", { "sketchPlane" : qUnion([Q0])});
            skCircle(sketch, "E72.0", {"center": v(-70.37, 88) * mm, "radius": 3 * mm});
            skCircle(sketch, "E73.0", {"center": v(-70.37, 88) * mm, "radius": 1.5 * mm});
            skLineSegment(sketch, "E74", {"start": v(-70.37, 85) * mm, "end": v(-73.95, 80.83) * mm});
            skLineSegment(sketch, "E75", {"start": v(-73.95, 80.83) * mm, "end": v(-85.94, 88.99) * mm});
            skLineSegment(sketch, "E76", {"start": v(-85.94, 88.99) * mm, "end": v(-86.37, 90.94) * mm});
            skLineSegment(sketch, "E77", {"start": v(-86.37, 90.94) * mm, "end": v(-74.78, 83.1) * mm});
            skLineSegment(sketch, "E78", {"start": v(-74.78, 83.1) * mm, "end": v(-72.43, 85.82) * mm});
            skSolve(sketch);
        }
        {
            var Q0;
            Q0=qSketchRegion(id+"F60",true);
            extrude(context, id + "F61", {"entities" : qUnion([Q0]), "endBound" : BoundingType.SYMMETRIC, "depth" : 2 * mm, "offsetDistance" : 25 * mm});
        }
        {
            var Q0;
            Q0=makeQuery(id+"F61.opExtrude","SWEPT_BODY",BODY,{"disambiguationData":[OSD([sQuery(id+"F60.wireOp",EDGE,"E72.0"),sQuery(id+"F60.wireOp",EDGE,"E73.0"),sQuery(id+"F60.wireOp",EDGE,"E74"),sQuery(id+"F60.wireOp",EDGE,"E75"),sQuery(id+"F60.wireOp",EDGE,"E76"),sQuery(id+"F60.wireOp",EDGE,"E77"),sQuery(id+"F60.wireOp",EDGE,"E78")])]});
            var Q1;
            Q1=qCreatedBy(makeId("Right.planeOp"),FACE);
            mirror(context, id + "F62", {"entities" : qUnion([Q0]), "mirrorPlane" : qUnion([Q1])});
        }
        {
            var Q0;
            {var subQ0=sQuery(id+"F30.wireOp",EDGE,"E29.top");var subQ2=sQuery(id+"F30.wireOp",EDGE,"E29.bottom");var subQ4=sQuery(id+"F30.wireOp",EDGE,"E29.right");var subQ5=makeQuery(id+"F31.opExtrude","SWEPT_FACE",FACE,{"disambiguationData":[OSD([subQ4])]});var subQ6=makeQuery(id+"F31.opExtrude","SWEPT_FACE",FACE,{"disambiguationData":[OSD([subQ2])]});var subQ10=sQuery(id+"F30.wireOp",EDGE,"E29.left");Q0=makeQuery(id+"F57.boolean.opBoolean","SPLIT",FACE,{"disambiguationData":[TD([subQ5])],"derivedFrom":makeQuery(id+"F51.boolean.opBoolean","SPLIT",FACE,{"disambiguationData":[TD([subQ6])],"derivedFrom":makeQuery(id+"F31.opExtrude","CAP_FACE",FACE,{"disambiguationData":[OSD([subQ2,subQ0,subQ10,subQ4])],"isStart":false})})});}
            var sketch = newSketch(context, id + "F63", { "sketchPlane" : qUnion([Q0])});
            skLineSegment(sketch, "E79.bottom", {"start": v(-7.5, 102) * mm, "end": v(-4.7, 102) * mm});
            skLineSegment(sketch, "E79.top", {"start": v(-7.5, 82) * mm, "end": v(-4.7, 82) * mm});
            skLineSegment(sketch, "E79.left", {"start": v(-7.5, 102) * mm, "end": v(-7.5, 82) * mm});
            skLineSegment(sketch, "E79.right", {"start": v(7.5, 102) * mm, "end": v(7.5, 82) * mm});
            skLineSegment(sketch, "E80", {"start": v(-4.7, 82) * mm, "end": v(-4.7, 87) * mm});
            skLineSegment(sketch, "E81", {"start": v(-2.2, 82) * mm, "end": v(-2.2, 87) * mm});
            skLineSegment(sketch, "E82", {"start": v(-2.2, 87) * mm, "end": v(-4.7, 87) * mm});
            skLineSegment(sketch, "E83", {"start": v(2.3, 82) * mm, "end": v(2.3, 87) * mm});
            skLineSegment(sketch, "E84", {"start": v(2.3, 87) * mm, "end": v(4.8, 87) * mm});
            skLineSegment(sketch, "E85", {"start": v(4.8, 87) * mm, "end": v(4.8, 82) * mm});
            skLineSegment(sketch, "E86", {"start": v(-4.7, 102) * mm, "end": v(-4.7, 97) * mm});
            skLineSegment(sketch, "E87", {"start": v(-4.7, 97) * mm, "end": v(-2.2, 97) * mm});
            skLineSegment(sketch, "E88", {"start": v(-2.2, 97) * mm, "end": v(-2.2, 102) * mm});
            skLineSegment(sketch, "E89", {"start": v(2.3, 102) * mm, "end": v(2.3, 97) * mm});
            skLineSegment(sketch, "E90", {"start": v(2.3, 97) * mm, "end": v(4.8, 97) * mm});
            skLineSegment(sketch, "E91", {"start": v(4.8, 97) * mm, "end": v(4.8, 102) * mm});
            skLineSegment(sketch, "E92.trimOffspring", {"start": v(-2.2, 102) * mm, "end": v(2.3, 102) * mm});
            skLineSegment(sketch, "E93.trimOffspring", {"start": v(4.8, 102) * mm, "end": v(7.5, 102) * mm});
            skLineSegment(sketch, "E94.trimOffspring", {"start": v(-2.2, 82) * mm, "end": v(2.3, 82) * mm});
            skLineSegment(sketch, "E95.trimOffspring", {"start": v(4.8, 82) * mm, "end": v(7.5, 82) * mm});
            skSolve(sketch);
        }
        {
            var Q0;
            Q0=qSketchRegion(id+"F63",true);
            extrude(context, id + "F64", {"entities" : qUnion([Q0]), "operationType" : NewBodyOperationType.ADD, "depth" : 1 * mm, "offsetDistance" : 25 * mm});
        }
        {
            var Q0;
            Q0=makeQuery(id+"F64.boolean.opBoolean","MERGE",EDGE,{"derivedFrom":[makeQuery(id+"F31.opExtrude","SWEPT_EDGE",EDGE,{"disambiguationData":[OSD([sQuery(id+"F30.wireOp",EDGE,"E29.top"),sQuery(id+"F30.wireOp",EDGE,"E29.left")])]}),makeQuery(id+"F64.opExtrude","SWEPT_EDGE",EDGE,{"disambiguationData":[OSD([sQuery(id+"F63.wireOp",EDGE,"E79.right"),sQuery(id+"F63.wireOp",EDGE,"E93.trimOffspring")])]})]});
            var Q1;
            Q1=makeQuery(id+"F64.boolean.opBoolean","MERGE",EDGE,{"derivedFrom":[makeQuery(id+"F31.opExtrude","SWEPT_EDGE",EDGE,{"disambiguationData":[OSD([sQuery(id+"F30.wireOp",EDGE,"E29.bottom"),sQuery(id+"F30.wireOp",EDGE,"E29.left")])]}),makeQuery(id+"F64.opExtrude","SWEPT_EDGE",EDGE,{"disambiguationData":[OSD([sQuery(id+"F63.wireOp",EDGE,"E79.right"),sQuery(id+"F63.wireOp",EDGE,"E95.trimOffspring")])]})]});
            var Q2;
            Q2=makeQuery(id+"F64.boolean.opBoolean","MERGE",EDGE,{"derivedFrom":[makeQuery(id+"F31.opExtrude","SWEPT_EDGE",EDGE,{"disambiguationData":[OSD([sQuery(id+"F30.wireOp",EDGE,"E29.top"),sQuery(id+"F30.wireOp",EDGE,"E29.right")])]}),makeQuery(id+"F64.opExtrude","SWEPT_EDGE",EDGE,{"disambiguationData":[OSD([sQuery(id+"F63.wireOp",EDGE,"E79.bottom"),sQuery(id+"F63.wireOp",EDGE,"E79.left")])]})]});
            var Q3;
            Q3=makeQuery(id+"F64.boolean.opBoolean","MERGE",EDGE,{"derivedFrom":[makeQuery(id+"F31.opExtrude","SWEPT_EDGE",EDGE,{"disambiguationData":[OSD([sQuery(id+"F30.wireOp",EDGE,"E29.bottom"),sQuery(id+"F30.wireOp",EDGE,"E29.right")])]}),makeQuery(id+"F64.opExtrude","SWEPT_EDGE",EDGE,{"disambiguationData":[OSD([sQuery(id+"F63.wireOp",EDGE,"E79.top"),sQuery(id+"F63.wireOp",EDGE,"E79.left")])]})]});
            var Q4;
            Q4=makeQuery(id+"F64.opExtrude","CAP_EDGE",EDGE,{"disambiguationData":[OSD([sQuery(id+"F63.wireOp",EDGE,"E79.right")])],"isStart":false});
            var Q5;
            Q5=makeQuery(id+"F55.opPattern","COPY",EDGE,{"derivedFrom":makeQuery(id+"F54.opExtrude","CAP_EDGE",EDGE,{"disambiguationData":[OSD([sQuery(id+"F53.wireOp",EDGE,"E62")])],"isStart":false}),"instanceName":"1"});
            var Q6;
            Q6=makeQuery(id+"F64.opExtrude","CAP_EDGE",EDGE,{"disambiguationData":[OSD([sQuery(id+"F63.wireOp",EDGE,"E79.left")])],"isStart":false});
            var Q7;
            Q7=makeQuery(id+"F55.opPattern","COPY",EDGE,{"derivedFrom":makeQuery(id+"F54.opExtrude","CAP_EDGE",EDGE,{"disambiguationData":[OSD([sQuery(id+"F53.wireOp",EDGE,"E62")])],"isStart":true}),"instanceName":"1"});
            var Q8;
            Q8=makeQuery(id+"F55.opPattern","COPY",EDGE,{"derivedFrom":makeQuery(id+"F54.opExtrude","SWEPT_EDGE",EDGE,{"disambiguationData":[OSD([sQuery(id+"F53.wireOp",EDGE,"E61"),sQuery(id+"F53.wireOp",EDGE,"E62")])]}),"instanceName":"1"});
            var Q9;
            Q9=makeQuery(id+"F54.opExtrude","SWEPT_EDGE",EDGE,{"disambiguationData":[OSD([sQuery(id+"F53.wireOp",EDGE,"E61"),sQuery(id+"F53.wireOp",EDGE,"E62")])]});
            var Q10;
            Q10=makeQuery(id+"F54.opExtrude","CAP_EDGE",EDGE,{"disambiguationData":[OSD([sQuery(id+"F53.wireOp",EDGE,"E62")])],"isStart":false});
            var Q11;
            Q11=makeQuery(id+"F54.opExtrude","CAP_EDGE",EDGE,{"disambiguationData":[OSD([sQuery(id+"F53.wireOp",EDGE,"E62")])],"isStart":true});
            var Q12;
            Q12=makeQuery(id+"F61.opExtrude","CAP_EDGE",EDGE,{"disambiguationData":[OSD([sQuery(id+"F60.wireOp",EDGE,"E75")])],"isStart":false});
            var Q13;
            Q13=makeQuery(id+"F61.opExtrude","CAP_EDGE",EDGE,{"disambiguationData":[OSD([sQuery(id+"F60.wireOp",EDGE,"E75")])],"isStart":true});
            var Q14;
            Q14=makeQuery(id+"F62.opPattern","COPY",EDGE,{"derivedFrom":makeQuery(id+"F61.opExtrude","CAP_EDGE",EDGE,{"disambiguationData":[OSD([sQuery(id+"F60.wireOp",EDGE,"E75")])],"isStart":true}),"instanceName":"1"});
            var Q15;
            Q15=makeQuery(id+"F62.opPattern","COPY",EDGE,{"derivedFrom":makeQuery(id+"F61.opExtrude","CAP_EDGE",EDGE,{"disambiguationData":[OSD([sQuery(id+"F60.wireOp",EDGE,"E75")])],"isStart":false}),"instanceName":"1"});
            var Q16;
            Q16=makeQuery(id+"F61.opExtrude","SWEPT_FACE",FACE,{"disambiguationData":[OSD([sQuery(id+"F60.wireOp",EDGE,"E75")])]});
            var Q17;
            Q17=makeQuery(id+"F62.opPattern","COPY",EDGE,{"derivedFrom":makeQuery(id+"F61.opExtrude","SWEPT_EDGE",EDGE,{"disambiguationData":[OSD([sQuery(id+"F60.wireOp",EDGE,"E74"),sQuery(id+"F60.wireOp",EDGE,"E75")])]}),"instanceName":"1"});
            var Q18;
            Q18=makeQuery(id+"F31.opExtrude","CAP_EDGE",EDGE,{"disambiguationData":[OSD([sQuery(id+"F30.wireOp",EDGE,"E29.top")])],"isStart":true});
            var Q19;
            Q19=makeQuery(id+"F31.opExtrude","CAP_EDGE",EDGE,{"disambiguationData":[OSD([sQuery(id+"F30.wireOp",EDGE,"E29.bottom")])],"isStart":true});
            var Q20;
            Q20=makeQuery(id+"F31.opExtrude","CAP_EDGE",EDGE,{"disambiguationData":[OSD([sQuery(id+"F30.wireOp",EDGE,"E29.left")])],"isStart":true});
            var Q21;
            Q21=makeQuery(id+"F31.opExtrude","CAP_EDGE",EDGE,{"disambiguationData":[OSD([sQuery(id+"F30.wireOp",EDGE,"E29.right")])],"isStart":true});
            fillet(context, id + "F65", {"entities" : qUnion([Q0, Q1, Q2, Q3, Q4, Q5, Q6, Q7, Q8, Q9, Q10, Q11, Q12, Q13, Q14, Q15, Q16, Q17, Q18, Q19, Q20, Q21]), "radius" : 1 * mm, "tangentPropagation" : true, "allowEdgeOverflow" : false});
        }
    });
